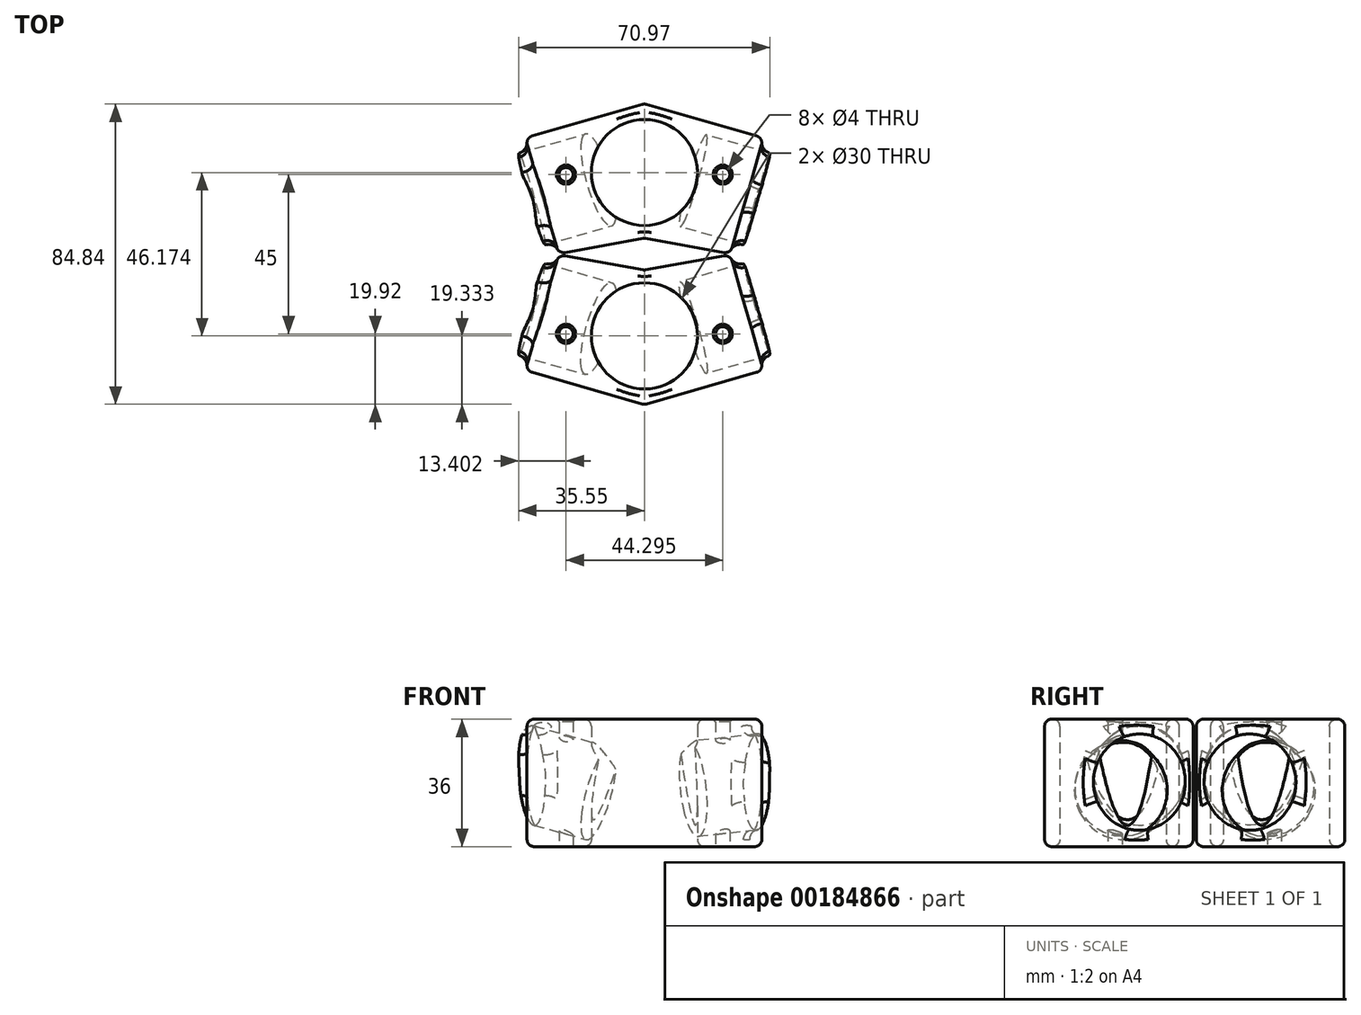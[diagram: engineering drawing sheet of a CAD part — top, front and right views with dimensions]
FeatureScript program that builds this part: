
annotation { "Feature Type Name" : "Feature", "Feature Type Description" : "" }
export const myFeature = defineFeature(function(context is Context, id is Id, definition is map)
    precondition{}
    {
        {
            var Q0;
            Q0=qCreatedBy(makeId("Top.planeOp"),FACE);
            var sketch = newSketch(context, id + "F0", { "sketchPlane" : qUnion([Q0])});
            skLineSegment(sketch, "E0", {"start": v(0, 0) * mm, "end": v(0, 20) * mm});
            skLineSegment(sketch, "E1", {"start": v(0, 0) * mm, "end": v(0, -18) * mm});
            skLineSegment(sketch, "E2", {"start": v(0, 20) * mm, "end": v(33.64, 10.35) * mm});
            skLineSegment(sketch, "E3", {"start": v(33.64, 10.35) * mm, "end": v(24.27, -22.33) * mm});
            skLineSegment(sketch, "E4", {"start": v(0, -18) * mm, "end": v(24.27, -22.33) * mm});
            skLineSegment(sketch, "E5.MirrorCS", {"start": v(0, 20) * mm, "end": v(-33.64, 10.35) * mm});
            skLineSegment(sketch, "E6.MirrorCS", {"start": v(-33.64, 10.35) * mm, "end": v(-24.27, -22.33) * mm});
            skLineSegment(sketch, "E7.MirrorCS", {"start": v(0, -18) * mm, "end": v(-24.27, -22.33) * mm});
            skCircle(sketch, "E8", {"center": v(0, 0.59) * mm, "radius": 15 * mm});
            skSolve(sketch);
        }
        {
            var Q0;
            Q0 = qSketchRegion(id + "F0", true);
            extrude(context, id + "F1", {"entities" : qUnion([Q0]), "depth" : 36 * mm});
        }
        {
            var Q0;
            Q0=makeQuery(id+"F1.opExtrude","CAP_FACE",FACE,{"disambiguationData":[OSD([sQuery(id+"F0.wireOp",EDGE,"E2"),sQuery(id+"F0.wireOp",EDGE,"E3"),sQuery(id+"F0.wireOp",EDGE,"E4"),sQuery(id+"F0.wireOp",EDGE,"E5.MirrorCS"),sQuery(id+"F0.wireOp",EDGE,"E6.MirrorCS"),sQuery(id+"F0.wireOp",EDGE,"E7.MirrorCS"),sQuery(id+"F0.wireOp",EDGE,"E8")])],"isStart":false});
            var Q1;
            Q1=makeQuery(id+"F1.opExtrude","CAP_FACE",FACE,{"disambiguationData":[OSD([sQuery(id+"F0.wireOp",EDGE,"E2"),sQuery(id+"F0.wireOp",EDGE,"E3"),sQuery(id+"F0.wireOp",EDGE,"E4"),sQuery(id+"F0.wireOp",EDGE,"E5.MirrorCS"),sQuery(id+"F0.wireOp",EDGE,"E6.MirrorCS"),sQuery(id+"F0.wireOp",EDGE,"E7.MirrorCS"),sQuery(id+"F0.wireOp",EDGE,"E8")])],"isStart":true});
            var Q2;
            Q2=makeQuery(id+"F1.opExtrude","SWEPT_EDGE",EDGE,{"disambiguationData":[OSD([sQuery(id+"F0.wireOp",EDGE,"E3"),sQuery(id+"F0.wireOp",EDGE,"E4")])]});
            var Q3;
            Q3=makeQuery(id+"F1.opExtrude","SWEPT_EDGE",EDGE,{"disambiguationData":[OSD([sQuery(id+"F0.wireOp",EDGE,"E2"),sQuery(id+"F0.wireOp",EDGE,"E3")])]});
            var Q4;
            Q4=makeQuery(id+"F1.opExtrude","SWEPT_EDGE",EDGE,{"disambiguationData":[OSD([sQuery(id+"F0.wireOp",EDGE,"E6.MirrorCS"),sQuery(id+"F0.wireOp",EDGE,"E7.MirrorCS")])]});
            var Q5;
            Q5=makeQuery(id+"F1.opExtrude","SWEPT_EDGE",EDGE,{"disambiguationData":[OSD([sQuery(id+"F0.wireOp",EDGE,"E5.MirrorCS"),sQuery(id+"F0.wireOp",EDGE,"E6.MirrorCS")])]});
            var Q6;
            Q6=makeQuery(id+"F1.opExtrude","SWEPT_EDGE",EDGE,{"disambiguationData":[OSD([sQuery(id+"F0.wireOp",EDGE,"E0"),sQuery(id+"F0.wireOp",EDGE,"E2"),sQuery(id+"F0.wireOp",EDGE,"E5.MirrorCS")])]});
            var Q7;
            Q7=makeQuery(id+"F1.opExtrude","SWEPT_EDGE",EDGE,{"disambiguationData":[OSD([sQuery(id+"F0.wireOp",EDGE,"E1"),sQuery(id+"F0.wireOp",EDGE,"E4"),sQuery(id+"F0.wireOp",EDGE,"E7.MirrorCS")])]});
            fillet(context, id + "F2", {"entities" : qUnion([Q0, Q1, Q2, Q3, Q4, Q5, Q6, Q7]), "radius" : 2 * mm, "tangentPropagation" : true, "allowEdgeOverflow" : false});
        }
        {
            var Q0;
            Q0=makeQuery(id+"F1.opExtrude","SWEPT_FACE",FACE,{"disambiguationData":[OSD([sQuery(id+"F0.wireOp",EDGE,"E3")])]});
            var sketch = newSketch(context, id + "F3", { "sketchPlane" : qUnion([Q0])});
            skCircle(sketch, "E9", {"center": v(2.13, 18) * mm, "radius": 13.5 * mm});
            skPoint(sketch, "E9.centerSnap0", {"position": v(-12.97, 18) * mm});
            skPoint(sketch, "E9.centerSnap1", {"position": v(2.13, 34) * mm});
            skSolve(sketch);
        }
        {
            var Q0;
            Q0 = qSketchRegion(id + "F3", true);
            extrude(context, id + "F4", {"entities" : qUnion([Q0]), "endBound" : BoundingType.SYMMETRIC, "depth" : 35 * mm});
        }
        {
            var Q0;
            Q0=makeQuery(id+"F4.opExtrude","SWEPT_BODY",BODY,{"disambiguationData":[OSD([sQuery(id+"F3.wireOp",EDGE,"E9")])]});
            var Q1;
            {var subQ0=sQuery(id+"F0.wireOp",EDGE,"E3");Q1=makeQuery(id+"F2.opFillet","BLEND_EDGE",EDGE,{"blendedFrom":[makeQuery(id+"F1.opExtrude","CAP_EDGE",EDGE,{"disambiguationData":[OSD([subQ0])],"isStart":false}),makeQuery(id+"F1.opExtrude","SWEPT_FACE",FACE,{"disambiguationData":[OSD([subQ0])]})],"blendedInto":[makeQuery(id+"F1.opExtrude","SWEPT_FACE",FACE,{"disambiguationData":[OSD([subQ0])]})]});}
            transform(context, id + "F5", {"entities" : qUnion([Q0]), "transformType" : TransformType.ROTATION, "transformAxis" : qUnion([Q1]), "angle" : 6 * degree, "makeCopy" : false});
        }
        {
            var Q0;
            Q0=makeQuery(id+"F1.opExtrude","SWEPT_FACE",FACE,{"disambiguationData":[OSD([sQuery(id+"F0.wireOp",EDGE,"E6.MirrorCS")])]});
            var sketch = newSketch(context, id + "F6", { "sketchPlane" : qUnion([Q0])});
            skCircle(sketch, "E10", {"center": v(-2.13, 18) * mm, "radius": 13.5 * mm});
            skPoint(sketch, "E10.centerSnap0", {"position": v(-17.23, 18) * mm});
            skPoint(sketch, "E10.centerSnap1", {"position": v(-2.13, 34) * mm});
            skSolve(sketch);
        }
        {
            var Q0;
            Q0 = qSketchRegion(id + "F6", true);
            extrude(context, id + "F7", {"entities" : qUnion([Q0]), "endBound" : BoundingType.SYMMETRIC, "depth" : 43 * mm});
        }
        {
            var Q0;
            Q0=makeQuery(id+"F7.opExtrude","SWEPT_BODY",BODY,{"disambiguationData":[OSD([sQuery(id+"F6.wireOp",EDGE,"E10")])]});
            var Q1;
            {var subQ0=sQuery(id+"F0.wireOp",EDGE,"E6.MirrorCS");Q1=makeQuery(id+"F2.opFillet","BLEND_EDGE",EDGE,{"blendedFrom":[makeQuery(id+"F1.opExtrude","CAP_EDGE",EDGE,{"disambiguationData":[OSD([subQ0])],"isStart":false}),makeQuery(id+"F1.opExtrude","SWEPT_FACE",FACE,{"disambiguationData":[OSD([subQ0])]})],"blendedInto":[makeQuery(id+"F1.opExtrude","SWEPT_FACE",FACE,{"disambiguationData":[OSD([subQ0])]})]});}
            transform(context, id + "F8", {"entities" : qUnion([Q0]), "transformType" : TransformType.ROTATION, "transformAxis" : qUnion([Q1]), "angle" : 345 * degree, "makeCopy" : false});
        }
        {
            var Q0;
            Q0=makeQuery(id+"F7.opExtrude","SWEPT_BODY",BODY,{"disambiguationData":[OSD([sQuery(id+"F6.wireOp",EDGE,"E10")])]});
            transform(context, id + "F9", {"entities" : qUnion([Q0]), "transformType" : TransformType.TRANSLATION_3D, "dx" : 0 * mm, "dy" : 0 * mm, "dz" : 2 * mm, "makeCopy" : false});
        }
        {
            var Q0;
            Q0=qCreatedBy(makeId("Top.planeOp"),FACE);
            var sketch = newSketch(context, id + "F10", { "sketchPlane" : qUnion([Q0])});
            skCircle(sketch, "E11", {"center": v(22.15, 0) * mm, "radius": 2 * mm});
            skCircle(sketch, "E12.MirrorC", {"center": v(-22.15, 0) * mm, "radius": 2 * mm});
            skSolve(sketch);
        }
        {
            var Q0;
            Q0 = qSketchRegion(id + "F10", true);
            extrude(context, id + "F11", {"entities" : qUnion([Q0]), "depth" : 40 * mm});
        }
        {
            var Q0;
            Q0=makeQuery(id+"F11.opExtrude","SWEPT_BODY",BODY,{"disambiguationData":[OSD([sQuery(id+"F10.wireOp",EDGE,"E11")])]});
            var Q1;
            Q1=makeQuery(id+"F11.opExtrude","SWEPT_BODY",BODY,{"disambiguationData":[OSD([sQuery(id+"F10.wireOp",EDGE,"E12.MirrorC")])]});
            var Q2;
            Q2=makeQuery(id+"F1.opExtrude","SWEPT_BODY",BODY,{"disambiguationData":[OSD([sQuery(id+"F0.wireOp",EDGE,"E2"),sQuery(id+"F0.wireOp",EDGE,"E3"),sQuery(id+"F0.wireOp",EDGE,"E4"),sQuery(id+"F0.wireOp",EDGE,"E5.MirrorCS"),sQuery(id+"F0.wireOp",EDGE,"E6.MirrorCS"),sQuery(id+"F0.wireOp",EDGE,"E7.MirrorCS"),sQuery(id+"F0.wireOp",EDGE,"E8")])]});
            booleanBodies(context, id + "F12", {"operationType" : BooleanOperationType.SUBTRACTION, "tools" : qUnion([Q0, Q1]), "targets" : qUnion([Q2])});
        }
        {
            var Q0;
            Q0=makeQuery(id+"F12.opBoolean","INTERSECT",EDGE,{"derivedFrom":[makeQuery(id+"F2.opFillet","SPLIT",FACE,{"disambiguationData":[OD(0.0)],"derivedFrom":makeQuery(id+"F1.opExtrude","CAP_FACE",FACE,{"disambiguationData":[OSD([sQuery(id+"F0.wireOp",EDGE,"E2"),sQuery(id+"F0.wireOp",EDGE,"E3"),sQuery(id+"F0.wireOp",EDGE,"E4"),sQuery(id+"F0.wireOp",EDGE,"E5.MirrorCS"),sQuery(id+"F0.wireOp",EDGE,"E6.MirrorCS"),sQuery(id+"F0.wireOp",EDGE,"E7.MirrorCS"),sQuery(id+"F0.wireOp",EDGE,"E8")])],"isStart":false})}),makeQuery(id+"F11.opExtrude","SWEPT_FACE",FACE,{"disambiguationData":[OSD([sQuery(id+"F10.wireOp",EDGE,"E11")])]})]});
            var Q1;
            Q1=makeQuery(id+"F12.opBoolean","INTERSECT",EDGE,{"derivedFrom":[makeQuery(id+"F2.opFillet","SPLIT",FACE,{"disambiguationData":[OD(1.0)],"derivedFrom":makeQuery(id+"F1.opExtrude","CAP_FACE",FACE,{"disambiguationData":[OSD([sQuery(id+"F0.wireOp",EDGE,"E2"),sQuery(id+"F0.wireOp",EDGE,"E3"),sQuery(id+"F0.wireOp",EDGE,"E4"),sQuery(id+"F0.wireOp",EDGE,"E5.MirrorCS"),sQuery(id+"F0.wireOp",EDGE,"E6.MirrorCS"),sQuery(id+"F0.wireOp",EDGE,"E7.MirrorCS"),sQuery(id+"F0.wireOp",EDGE,"E8")])],"isStart":false})}),makeQuery(id+"F11.opExtrude","SWEPT_FACE",FACE,{"disambiguationData":[OSD([sQuery(id+"F10.wireOp",EDGE,"E12.MirrorC")])]})]});
            var Q2;
            Q2=makeQuery(id+"F12.opBoolean","COPY",EDGE,{"derivedFrom":makeQuery(id+"F11.opExtrude","CAP_EDGE",EDGE,{"disambiguationData":[OSD([sQuery(id+"F10.wireOp",EDGE,"E12.MirrorC")])],"isStart":true})});
            var Q3;
            Q3=makeQuery(id+"F12.opBoolean","COPY",EDGE,{"derivedFrom":makeQuery(id+"F11.opExtrude","CAP_EDGE",EDGE,{"disambiguationData":[OSD([sQuery(id+"F10.wireOp",EDGE,"E11")])],"isStart":true})});
            chamfer(context, id + "F13", {"entities" : qUnion([Q0, Q1, Q2, Q3]), "width" : .7 * mm, "tangentPropagation" : true});
        }
        {
            var Q0;
            Q0=makeQuery(id+"F4.opExtrude","SWEPT_BODY",BODY,{"disambiguationData":[OSD([sQuery(id+"F3.wireOp",EDGE,"E9")])]});
            transform(context, id + "F14", {"entities" : qUnion([Q0]), "transformType" : TransformType.TRANSLATION_3D, "dx" : 0 * mm, "dy" : 0 * mm, "dz" : 0 * mm, "makeCopy" : true});
        }
        {
            var Q0;
            Q0=makeQuery(id+"F7.opExtrude","SWEPT_BODY",BODY,{"disambiguationData":[OSD([sQuery(id+"F6.wireOp",EDGE,"E10")])]});
            transform(context, id + "F15", {"entities" : qUnion([Q0]), "transformType" : TransformType.TRANSLATION_3D, "dx" : 0 * mm, "dy" : 0 * mm, "dz" : 0 * mm, "makeCopy" : true});
        }
        {
            var Q0;
            Q0=makeQuery(id+"F1.opExtrude","SWEPT_BODY",BODY,{"disambiguationData":[OSD([sQuery(id+"F0.wireOp",EDGE,"E2"),sQuery(id+"F0.wireOp",EDGE,"E3"),sQuery(id+"F0.wireOp",EDGE,"E4"),sQuery(id+"F0.wireOp",EDGE,"E5.MirrorCS"),sQuery(id+"F0.wireOp",EDGE,"E6.MirrorCS"),sQuery(id+"F0.wireOp",EDGE,"E7.MirrorCS"),sQuery(id+"F0.wireOp",EDGE,"E8")])]});
            var Q1;
            Q1=makeQuery(id+"F4.opExtrude","SWEPT_BODY",BODY,{"disambiguationData":[OSD([sQuery(id+"F3.wireOp",EDGE,"E9")])]});
            var Q2;
            Q2=makeQuery(id+"F7.opExtrude","SWEPT_BODY",BODY,{"disambiguationData":[OSD([sQuery(id+"F6.wireOp",EDGE,"E10")])]});
            booleanBodies(context, id + "F16", {"operationType" : BooleanOperationType.UNION, "tools" : qUnion([Q0, Q1, Q2])});
        }
        {
            var Q0;
            Q0=makeQuery(id+"F16.opBoolean","INTERSECT",EDGE,{"derivedFrom":[makeQuery(id+"F1.opExtrude","SWEPT_FACE",FACE,{"disambiguationData":[OSD([sQuery(id+"F0.wireOp",EDGE,"E6.MirrorCS")])]}),makeQuery(id+"F7.opExtrude","SWEPT_FACE",FACE,{"disambiguationData":[OSD([sQuery(id+"F6.wireOp",EDGE,"E10")])]})]});
            var Q1;
            Q1=makeQuery(id+"F16.opBoolean","INTERSECT",EDGE,{"derivedFrom":[makeQuery(id+"F1.opExtrude","SWEPT_FACE",FACE,{"disambiguationData":[OSD([sQuery(id+"F0.wireOp",EDGE,"E3")])]}),makeQuery(id+"F4.opExtrude","SWEPT_FACE",FACE,{"disambiguationData":[OSD([sQuery(id+"F3.wireOp",EDGE,"E9")])]})]});
            fillet(context, id + "F17", {"entities" : qUnion([Q0, Q1]), "radius" : 3 * mm, "tangentPropagation" : true, "allowEdgeOverflow" : false});
        }
        {
            var Q0;
            Q0=makeQuery(id+"F14.opPattern","COPY",BODY,{"derivedFrom":makeQuery(id+"F4.opExtrude","SWEPT_BODY",BODY,{"disambiguationData":[OSD([sQuery(id+"F3.wireOp",EDGE,"E9")])]}),"instanceName":"1"});
            var Q1;
            Q1=makeQuery(id+"F15.opPattern","COPY",BODY,{"derivedFrom":makeQuery(id+"F7.opExtrude","SWEPT_BODY",BODY,{"disambiguationData":[OSD([sQuery(id+"F6.wireOp",EDGE,"E10")])]}),"instanceName":"1"});
            var Q2;
            Q2=makeQuery(id+"F1.opExtrude","SWEPT_BODY",BODY,{"disambiguationData":[OSD([sQuery(id+"F0.wireOp",EDGE,"E2"),sQuery(id+"F0.wireOp",EDGE,"E3"),sQuery(id+"F0.wireOp",EDGE,"E4"),sQuery(id+"F0.wireOp",EDGE,"E5.MirrorCS"),sQuery(id+"F0.wireOp",EDGE,"E6.MirrorCS"),sQuery(id+"F0.wireOp",EDGE,"E7.MirrorCS"),sQuery(id+"F0.wireOp",EDGE,"E8")])]});
            booleanBodies(context, id + "F18", {"operationType" : BooleanOperationType.SUBTRACTION, "tools" : qUnion([Q0, Q1]), "targets" : qUnion([Q2])});
        }
        {
            var Q0;
            Q0=makeQuery(id+"F1.opExtrude","SWEPT_BODY",BODY,{"disambiguationData":[OSD([sQuery(id+"F0.wireOp",EDGE,"E2"),sQuery(id+"F0.wireOp",EDGE,"E3"),sQuery(id+"F0.wireOp",EDGE,"E4"),sQuery(id+"F0.wireOp",EDGE,"E5.MirrorCS"),sQuery(id+"F0.wireOp",EDGE,"E6.MirrorCS"),sQuery(id+"F0.wireOp",EDGE,"E7.MirrorCS"),sQuery(id+"F0.wireOp",EDGE,"E8")])]});
            var Q1;
            Q1=qCreatedBy(makeId("Front.planeOp"),FACE);
            mirror(context, id + "F19", {"entities" : qUnion([Q0]), "mirrorPlane" : qUnion([Q1])});
        }
        {
            var Q0;
            Q0=makeQuery(id+"F19.opPattern","COPY",BODY,{"derivedFrom":makeQuery(id+"F1.opExtrude","SWEPT_BODY",BODY,{"disambiguationData":[OSD([sQuery(id+"F0.wireOp",EDGE,"E2"),sQuery(id+"F0.wireOp",EDGE,"E3"),sQuery(id+"F0.wireOp",EDGE,"E4"),sQuery(id+"F0.wireOp",EDGE,"E5.MirrorCS"),sQuery(id+"F0.wireOp",EDGE,"E6.MirrorCS"),sQuery(id+"F0.wireOp",EDGE,"E7.MirrorCS"),sQuery(id+"F0.wireOp",EDGE,"E8")])]}),"instanceName":"1"});
            transform(context, id + "F20", {"entities" : qUnion([Q0]), "transformType" : TransformType.TRANSLATION_3D, "dx" : 0 * mm, "dy" : -45 * mm, "dz" : 0 * mm, "makeCopy" : false});
        }
    });
